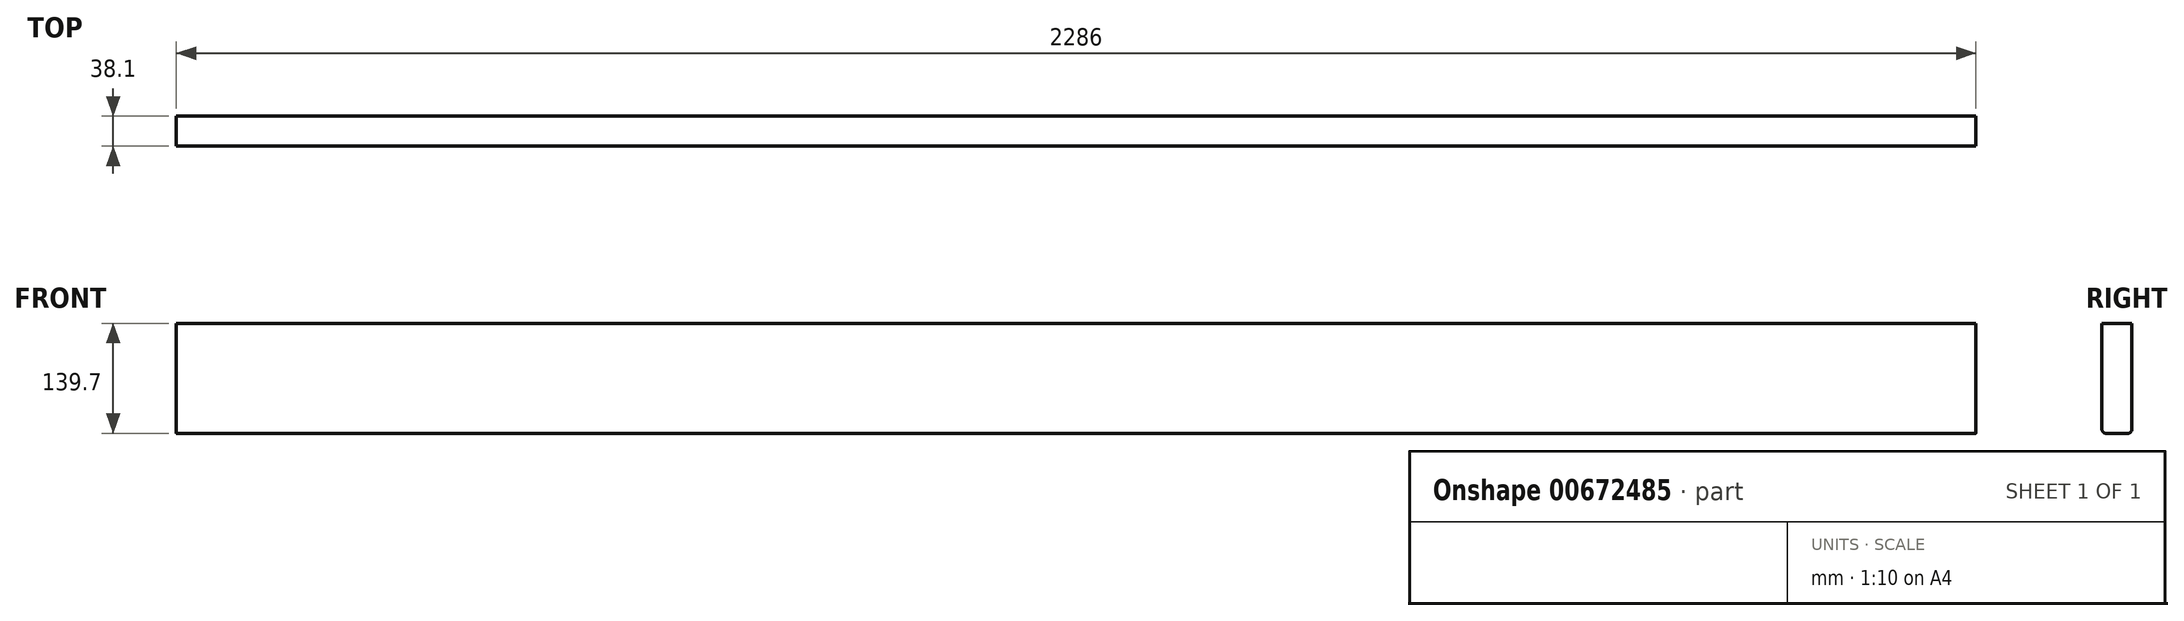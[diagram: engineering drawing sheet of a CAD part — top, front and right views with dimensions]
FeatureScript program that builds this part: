
annotation { "Feature Type Name" : "Feature", "Feature Type Description" : "" }
export const myFeature = defineFeature(function(context is Context, id is Id, definition is map)
    precondition{}
    {
        {
            var Q0;
            Q0=qCreatedBy(makeId("Front.planeOp"),FACE);
            var sketch = newSketch(context, id + "F0", { "sketchPlane" : qUnion([Q0])});
            skLineSegment(sketch, "E0.bottom", {"start": v(-1143, 69.85) * mm, "end": v(1143, 69.85) * mm});
            skLineSegment(sketch, "E0.top", {"start": v(-1143, -69.85) * mm, "end": v(1143, -69.85) * mm});
            skLineSegment(sketch, "E0.left", {"start": v(-1143, 69.85) * mm, "end": v(-1143, -69.85) * mm});
            skLineSegment(sketch, "E0.right", {"start": v(1143, 69.85) * mm, "end": v(1143, -69.85) * mm});
            skSolve(sketch);
        }
        {
            var Q0;
            Q0=makeQuery(id+"F0.imprint","IMPRINT",FACE,{"disambiguationData":[TD([[makeQuery(id+"F0.imprint","IMPRINT",EDGE,{"derivedFrom":sQuery(id+"F0.wireOp",EDGE,"E0.bottom")}),-1.0]])]});
            extrude(context, id + "F1", {"entities" : qUnion([Q0]), "depth" : 19.05 * mm, "offsetDistance" : 25.4 * mm, "hasSecondDirection" : true, "secondDirectionOppositeDirection" : true, "secondDirectionDepth" : 19.05 * mm});
        }
        {
            var Q0;
            Q0=makeQuery(id+"F1.opExtrude","CAP_EDGE",EDGE,{"disambiguationData":[OSD([sQuery(id+"F0.wireOp",EDGE,"E0.top")])],"isStart":false});
            var Q1;
            Q1=makeQuery(id+"F1.opExtrude","CAP_EDGE",EDGE,{"disambiguationData":[OSD([sQuery(id+"F0.wireOp",EDGE,"E0.top")])],"isStart":true});
            fillet(context, id + "F2", {"entities" : qUnion([Q0, Q1]), "radius" : 5.08 * mm, "tangentPropagation" : true, "allowEdgeOverflow" : false});
        }
    });
